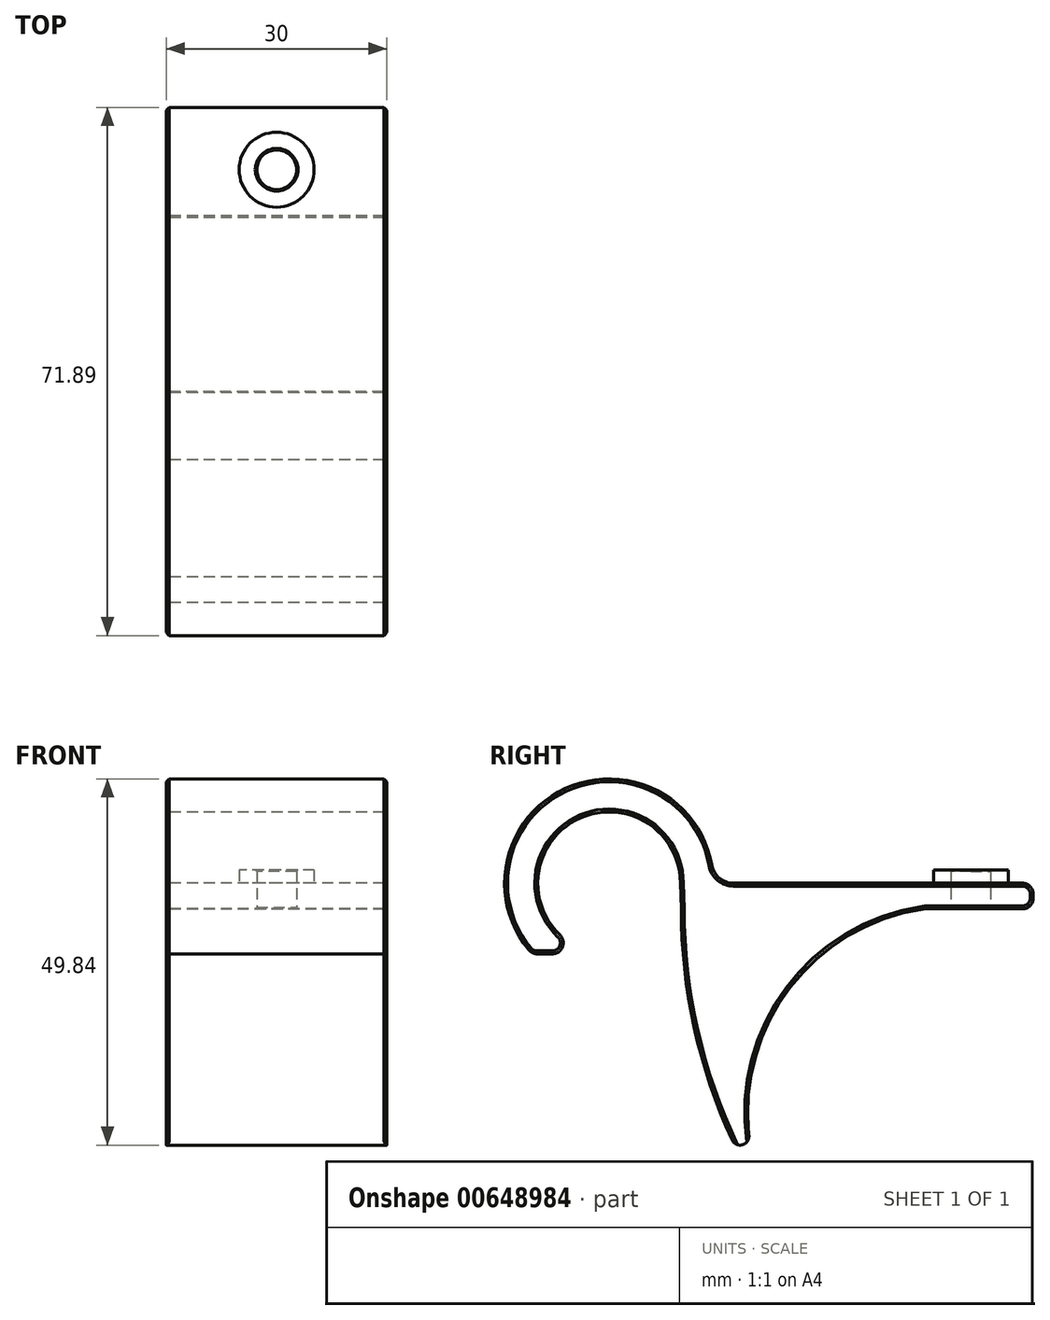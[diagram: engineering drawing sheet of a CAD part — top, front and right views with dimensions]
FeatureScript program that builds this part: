
annotation { "Feature Type Name" : "Feature", "Feature Type Description" : "" }
export const myFeature = defineFeature(function(context is Context, id is Id, definition is map)
    precondition{}
    {
        {
            var Q0;
            Q0=qCreatedBy(makeId("Right.planeOp"),FACE);
            var sketch = newSketch(context, id + "F0", { "sketchPlane" : qUnion([Q0])});
            skCircle(sketch, "E0", {"center": v(0, 0) * mm, "radius": 9.7 * mm});
            skLineSegment(sketch, "E1", {"start": v(9.7, 0) * mm, "end": v(57.69, 0) * mm});
            skLineSegment(sketch, "E2", {"start": v(9.7, 0) * mm, "end": v(9.82, -3.5) * mm});
            skLineSegment(sketch, "E3", {"start": v(84.82, -3.5) * mm, "end": v(-9.05, -3.5) * mm});
            skCircle(sketch, "E4.0", {"center": v(0, 0) * mm, "radius": 14.2 * mm});
            skLineSegment(sketch, "E5", {"start": v(-9.05, -3.5) * mm, "end": v(-13.76, -3.5) * mm});
            skLineSegment(sketch, "E6", {"start": v(-10.45, -9.6) * mm, "end": v(-1.32, -9.6) * mm});
            skPoint(sketch, "E7.second.point", {"position": v(159.82, -3.5) * mm});
            skPoint(sketch, "E7.third.point", {"position": v(54.55, -52.77) * mm});
            skArc(sketch, "E8.trimOffspring", {"start": v(9.82, -3.5) * mm, "mid": v(13.36, -26.27) * mm, "end": v(23.65, -46.89) * mm});
            skPoint(sketch, "E9", {"position": v(51.34, -12.7) * mm});
            skArc(sketch, "E10", {"start": v(42.78, -3.5) * mm, "mid": v(21.22, -19.9) * mm, "end": v(23.65, -46.89) * mm});
            skLineSegment(sketch, "E11", {"start": v(57.69, 0) * mm, "end": v(57.69, -3.5) * mm});
            skPoint(sketch, "E12", {"position": v(50.33, -3.5) * mm});
            skPoint(sketch, "E13.start.orphan", {"position": v(105.68, 0) * mm});
            skPoint(sketch, "E14.orphan", {"position": v(109.7, -3.5) * mm});
            skSolve(sketch);
        }
        {
            var Q0;
            {var subQ3=sQuery(id+"F0.wireOp",EDGE,"E5");Q0=makeQuery(id+"F0.imprint","IMPRINT",FACE,{"disambiguationData":[TD([[makeQuery(id+"F0.imprint","IMPRINT",EDGE,{"derivedFrom":subQ3}),-1.0]])]});}
            var Q1;
            {var subQ0=sQuery(id+"F0.wireOp",EDGE,"E2");Q1=makeQuery(id+"F0.imprint","IMPRINT",FACE,{"disambiguationData":[TD([[makeQuery(id+"F0.imprint","IMPRINT",EDGE,{"derivedFrom":subQ0}),1.0]])]});}
            var Q2;
            {var subQ0=sQuery(id+"F0.wireOp",EDGE,"E5");Q2=makeQuery(id+"F0.imprint","IMPRINT",FACE,{"disambiguationData":[TD([[makeQuery(id+"F0.imprint","IMPRINT",EDGE,{"derivedFrom":subQ0}),1.0]])]});}
            var Q3;
            {var subQ0=sQuery(id+"F0.wireOp",EDGE,"E8.trimOffspring");var subQ3=sQuery(id+"F0.wireOp",EDGE,"E4.0");var subQ5=makeQuery(id+"F0.imprint","INTERSECT",VERTEX,{"derivedFrom":[subQ3,subQ0]});Q3=makeQuery(id+"F0.imprint","IMPRINT",FACE,{"disambiguationData":[TD([[makeQuery(id+"F0.imprint","IMPRINT",EDGE,{"disambiguationData":[TD([[subQ5,-1.0]])],"derivedFrom":subQ3}),1.0]])]});}
            var Q4;
            {var subQ0=sQuery(id+"F0.wireOp",EDGE,"E10");Q4=makeQuery(id+"F0.imprint","IMPRINT",FACE,{"disambiguationData":[TD([[makeQuery(id+"F0.imprint","IMPRINT",EDGE,{"derivedFrom":subQ0}),-1.0]])]});}
            var Q5;
            {var subQ0=sQuery(id+"F0.wireOp",EDGE,"E10");var subQ1=sQuery(id+"F0.wireOp",EDGE,"E3");var subQ3=makeQuery(id+"F0.imprint","INTERSECT",VERTEX,{"derivedFrom":[subQ1,subQ0]});Q5=makeQuery(id+"F0.imprint","IMPRINT",FACE,{"disambiguationData":[TD([[makeQuery(id+"F0.imprint","IMPRINT",EDGE,{"disambiguationData":[TD([[subQ3,1.0]])],"derivedFrom":subQ1}),-1.0]])]});}
            var Q6;
            {var subQ8=sQuery(id+"F0.wireOp",EDGE,"E11");Q6=makeQuery(id+"F0.imprint","IMPRINT",FACE,{"disambiguationData":[TD([[makeQuery(id+"F0.imprint","IMPRINT",EDGE,{"derivedFrom":subQ8}),-1.0]])]});}
            extrude(context, id + "F1", {"entities" : qUnion([Q0, Q1, Q2, Q3, Q4, Q5, Q6]), "depth" : 30 * mm, "offsetDistance" : 25 * mm});
        }
        {
            var Q0;
            Q0=makeQuery(id+"F1.opExtrude","SWEPT_FACE",FACE,{"disambiguationData":[OSD([sQuery(id+"F0.wireOp",EDGE,"E1")])]});
            var sketch = newSketch(context, id + "F2", { "sketchPlane" : qUnion([Q0])});
            skCircle(sketch, "E15", {"center": v(15, 49.2) * mm, "radius": 2.7 * mm});
            skCircle(sketch, "E16", {"center": v(15, 49.2) * mm, "radius": 5.1 * mm});
            skSolve(sketch);
        }
        {
            var Q0;
            Q0=makeQuery(id+"F2.imprint","IMPRINT",FACE,{"disambiguationData":[TD([[makeQuery(id+"F2.imprint","IMPRINT",EDGE,{"derivedFrom":sQuery(id+"F2.wireOp",EDGE,"E15")}),-1.0]])]});
            extrude(context, id + "F3", {"entities" : qUnion([Q0]), "operationType" : NewBodyOperationType.ADD, "depth" : 1.8 * mm, "offsetDistance" : 25 * mm});
        }
        {
            var Q0;
            Q0=makeQuery(id+"F3.boolean.opBoolean","SPLIT",FACE,{"disambiguationData":[TD([makeQuery(id+"F3.opExtrude","SWEPT_FACE",FACE,{"disambiguationData":[OSD([sQuery(id+"F2.wireOp",EDGE,"E15")])]})])],"derivedFrom":makeQuery(id+"F1.opExtrude","SWEPT_FACE",FACE,{"disambiguationData":[OSD([sQuery(id+"F0.wireOp",EDGE,"E1")])]})});
            extrude(context, id + "F4", {"entities" : qUnion([Q0]), "operationType" : NewBodyOperationType.REMOVE, "oppositeDirection" : true, "depth" : 25 * mm, "offsetDistance" : 25 * mm});
        }
        {
            var Q0;
            Q0=makeQuery(id+"F1.opExtrude","SWEPT_EDGE",EDGE,{"disambiguationData":[OSD([sQuery(id+"F0.wireOp",EDGE,"E1"),sQuery(id+"F0.wireOp",EDGE,"E4.0")])]});
            fillet(context, id + "F5", {"entities" : qUnion([Q0]), "radius" : 3 * mm, "tangentPropagation" : true, "allowEdgeOverflow" : false});
        }
        {
            var Q0;
            Q0=makeQuery(id+"F3.opExtrude","CAP_EDGE",EDGE,{"disambiguationData":[OSD([sQuery(id+"F2.wireOp",EDGE,"E16")])],"isStart":true});
            var Q1;
            Q1=makeQuery(id+"F1.opExtrude","SWEPT_EDGE",EDGE,{"disambiguationData":[OSD([sQuery(id+"F0.wireOp",EDGE,"E3"),sQuery(id+"F0.wireOp",EDGE,"E10")])]});
            chamfer(context, id + "F6", {"entities" : qUnion([Q0, Q1]), "width" : 1.8 * mm, "tangentPropagation" : true});
        }
        {
            var Q0;
            Q0=makeQuery(id+"F1.opExtrude","SWEPT_EDGE",EDGE,{"disambiguationData":[OSD([sQuery(id+"F0.wireOp",EDGE,"E1"),sQuery(id+"F0.wireOp",EDGE,"E11")])]});
            var Q1;
            Q1=makeQuery(id+"F1.opExtrude","SWEPT_EDGE",EDGE,{"disambiguationData":[OSD([sQuery(id+"F0.wireOp",EDGE,"E2"),sQuery(id+"F0.wireOp",EDGE,"E3"),sQuery(id+"F0.wireOp",EDGE,"E8.trimOffspring")])]});
            var Q2;
            Q2=makeQuery(id+"F1.opExtrude","SWEPT_EDGE",EDGE,{"disambiguationData":[OSD([sQuery(id+"F0.wireOp",EDGE,"E3"),sQuery(id+"F0.wireOp",EDGE,"E11")])]});
            var Q3;
            Q3=makeQuery(id+"F1.opExtrude","SWEPT_EDGE",EDGE,{"disambiguationData":[OSD([sQuery(id+"F0.wireOp",EDGE,"E0"),sQuery(id+"F0.wireOp",EDGE,"E6")])]});
            var Q4;
            Q4=makeQuery(id+"F1.opExtrude","SWEPT_EDGE",EDGE,{"disambiguationData":[OSD([sQuery(id+"F0.wireOp",EDGE,"E4.0"),sQuery(id+"F0.wireOp",EDGE,"E6")])]});
            fillet(context, id + "F7", {"entities" : qUnion([Q0, Q1, Q2, Q3, Q4]), "radius" : 1.5 * mm, "tangentPropagation" : true, "allowEdgeOverflow" : false});
        }
        {
            var Q0;
            Q0=makeQuery(id+"F1.opExtrude","CAP_FACE",FACE,{"disambiguationData":[OSD([sQuery(id+"F0.wireOp",EDGE,"E0"),sQuery(id+"F0.wireOp",EDGE,"E1"),sQuery(id+"F0.wireOp",EDGE,"E2"),sQuery(id+"F0.wireOp",EDGE,"E3"),sQuery(id+"F0.wireOp",EDGE,"E4.0"),sQuery(id+"F0.wireOp",EDGE,"E6"),sQuery(id+"F0.wireOp",EDGE,"E8.trimOffspring"),sQuery(id+"F0.wireOp",EDGE,"mrHWne4S-whD2-22Nn-zpoz-sdssya80vf21"),sQuery(id+"F0.wireOp",EDGE,"E10")])],"isStart":true});
            var Q1;
            Q1=makeQuery(id+"F1.opExtrude","CAP_FACE",FACE,{"disambiguationData":[OSD([sQuery(id+"F0.wireOp",EDGE,"E0"),sQuery(id+"F0.wireOp",EDGE,"E1"),sQuery(id+"F0.wireOp",EDGE,"E2"),sQuery(id+"F0.wireOp",EDGE,"E3"),sQuery(id+"F0.wireOp",EDGE,"E4.0"),sQuery(id+"F0.wireOp",EDGE,"E6"),sQuery(id+"F0.wireOp",EDGE,"E8.trimOffspring"),sQuery(id+"F0.wireOp",EDGE,"mrHWne4S-whD2-22Nn-zpoz-sdssya80vf21"),sQuery(id+"F0.wireOp",EDGE,"E10")])],"isStart":false});
            chamfer(context, id + "F8", {"entities" : qUnion([Q0, Q1]), "width" : 0.4 * mm, "tangentPropagation" : true});
        }
        {
            var Q0;
            Q0=makeQuery(id+"F1.opExtrude","SWEPT_EDGE",EDGE,{"disambiguationData":[OSD([sQuery(id+"F0.wireOp",EDGE,"E8.trimOffspring"),sQuery(id+"F0.wireOp",EDGE,"E10")])]});
            fillet(context, id + "F9", {"entities" : qUnion([Q0]), "radius" : 1.2 * mm, "tangentPropagation" : true, "allowEdgeOverflow" : false});
        }
        {
            var Q0;
            Q0=makeQuery(id+"F4.boolean.opBoolean","INTERSECT",EDGE,{"derivedFrom":[makeQuery(id+"F1.opExtrude","SWEPT_FACE",FACE,{"disambiguationData":[OSD([sQuery(id+"F0.wireOp",EDGE,"E3")])]}),makeQuery(id+"F4.opExtrude","SWEPT_FACE",FACE,{"disambiguationData":[OSD([sQuery(id+"F2.wireOp",EDGE,"E15")])]})]});
            var Q1;
            Q1=makeQuery(id+"F3.opExtrude","CAP_EDGE",EDGE,{"disambiguationData":[OSD([sQuery(id+"F2.wireOp",EDGE,"E15")])],"isStart":false});
            chamfer(context, id + "F10", {"entities" : qUnion([Q0, Q1]), "width" : 0.2 * mm, "tangentPropagation" : true});
        }
    });
